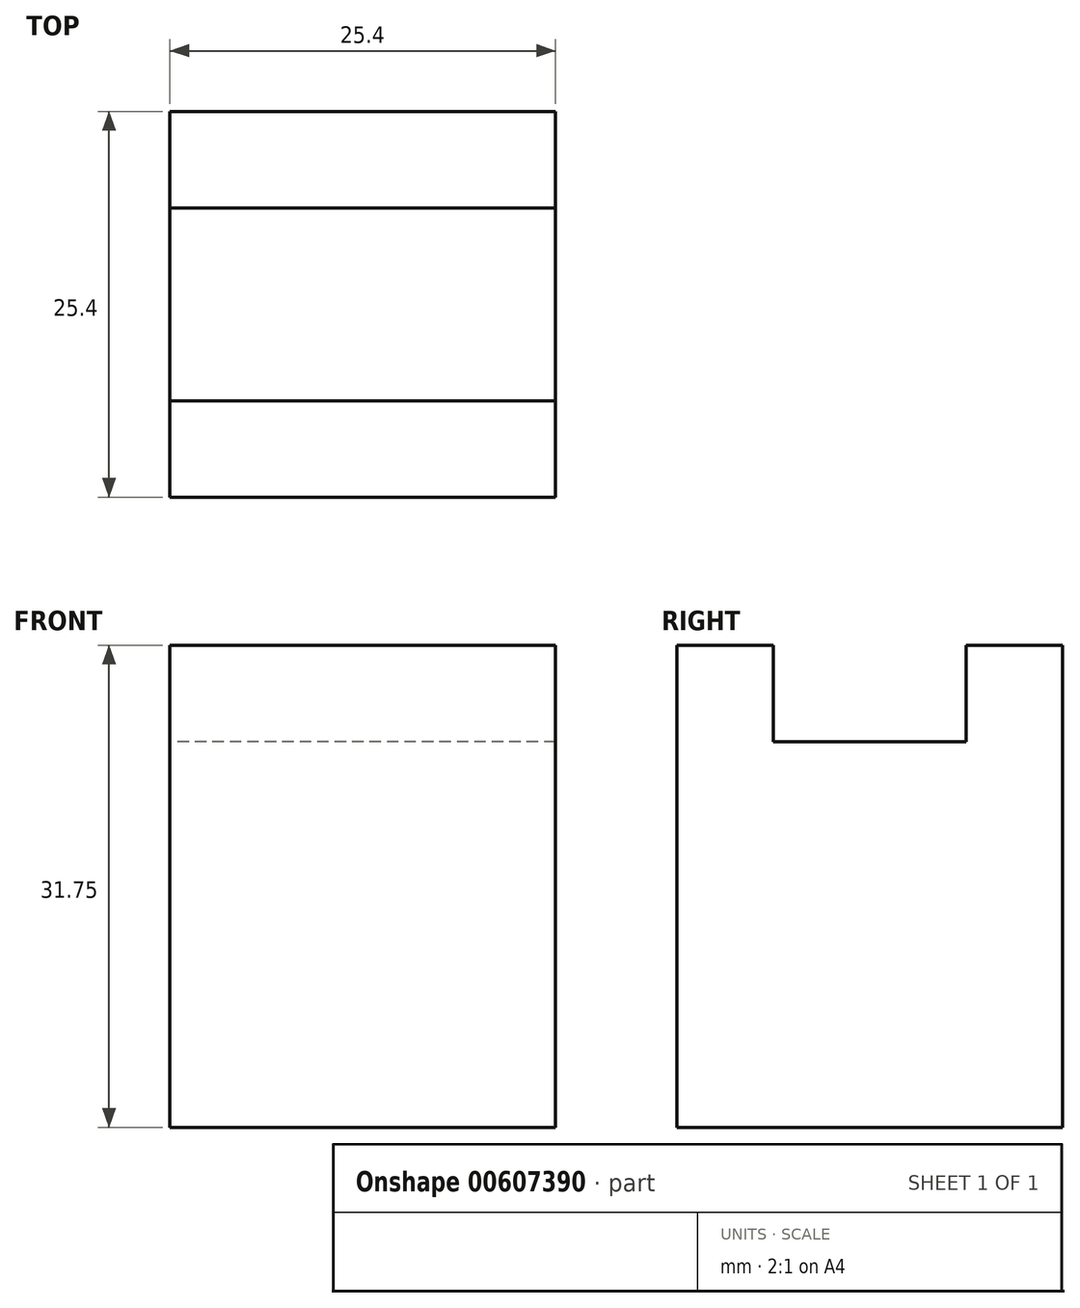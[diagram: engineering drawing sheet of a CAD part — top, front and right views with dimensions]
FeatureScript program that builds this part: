
annotation { "Feature Type Name" : "Feature", "Feature Type Description" : "" }
export const myFeature = defineFeature(function(context is Context, id is Id, definition is map)
    precondition{}
    {
        {
            var Q0;
            Q0=qCreatedBy(makeId("Right.planeOp"),FACE);
            var sketch = newSketch(context, id + "F0", { "sketchPlane" : qUnion([Q0])});
            skLineSegment(sketch, "E0", {"start": v(-12.7, 0) * mm, "end": v(12.7, 0) * mm});
            skLineSegment(sketch, "E1", {"start": v(-12.7, 0) * mm, "end": v(-12.7, 31.75) * mm});
            skLineSegment(sketch, "E2", {"start": v(12.7, 0) * mm, "end": v(12.7, 31.75) * mm});
            skLineSegment(sketch, "E3", {"start": v(12.7, 31.75) * mm, "end": v(6.35, 31.75) * mm});
            skLineSegment(sketch, "E4", {"start": v(-12.7, 31.75) * mm, "end": v(-6.35, 31.75) * mm});
            skLineSegment(sketch, "E5", {"start": v(-6.35, 31.75) * mm, "end": v(-6.35, 25.4) * mm});
            skLineSegment(sketch, "E6", {"start": v(6.35, 31.75) * mm, "end": v(6.35, 25.4) * mm});
            skLineSegment(sketch, "E7", {"start": v(-6.35, 25.4) * mm, "end": v(6.35, 25.4) * mm});
            skSolve(sketch);
        }
        {
            var Q0;
            Q0=qCreatedBy(makeId("Right.planeOp"),FACE);
            var sketch = newSketch(context, id + "F1", { "sketchPlane" : qUnion([Q0])});
            skLineSegment(sketch, "E8", {"start": v(-12.7, 0) * mm, "end": v(12.7, 0) * mm});
            skLineSegment(sketch, "E9", {"start": v(-12.7, 0) * mm, "end": v(-12.7, 31.75) * mm});
            skLineSegment(sketch, "E10", {"start": v(-12.7, 31.75) * mm, "end": v(-6.35, 31.75) * mm});
            skLineSegment(sketch, "E11", {"start": v(-6.35, 31.75) * mm, "end": v(-6.35, 25.4) * mm});
            skLineSegment(sketch, "E12", {"start": v(-6.35, 25.4) * mm, "end": v(6.35, 25.4) * mm});
            skLineSegment(sketch, "E13", {"start": v(6.35, 25.4) * mm, "end": v(6.35, 31.75) * mm});
            skLineSegment(sketch, "E14", {"start": v(6.35, 31.75) * mm, "end": v(12.7, 31.75) * mm});
            skLineSegment(sketch, "E15", {"start": v(12.7, 31.75) * mm, "end": v(12.7, 0) * mm});
            skSolve(sketch);
        }
        {
            var Q0;
            Q0=makeQuery(id+"F0.imprint","IMPRINT",FACE,{"disambiguationData":[TD([[makeQuery(id+"F0.imprint","IMPRINT",EDGE,{"derivedFrom":sQuery(id+"F0.wireOp",EDGE,"E0")}),1.0]])]});
            extrude(context, id + "F2", {"entities" : qUnion([Q0]), "depth" : 12.7 * mm, "offsetDistance" : 25.4 * mm});
        }
        {
            var Q0;
            Q0=makeQuery(id+"F1.imprint","IMPRINT",FACE,{"disambiguationData":[TD([[makeQuery(id+"F1.imprint","IMPRINT",EDGE,{"derivedFrom":sQuery(id+"F1.wireOp",EDGE,"E8")}),1.0]])]});
            extrude(context, id + "F3", {"entities" : qUnion([Q0]), "operationType" : NewBodyOperationType.ADD, "oppositeDirection" : true, "depth" : 12.7 * mm, "offsetDistance" : 25.4 * mm});
        }
    });
